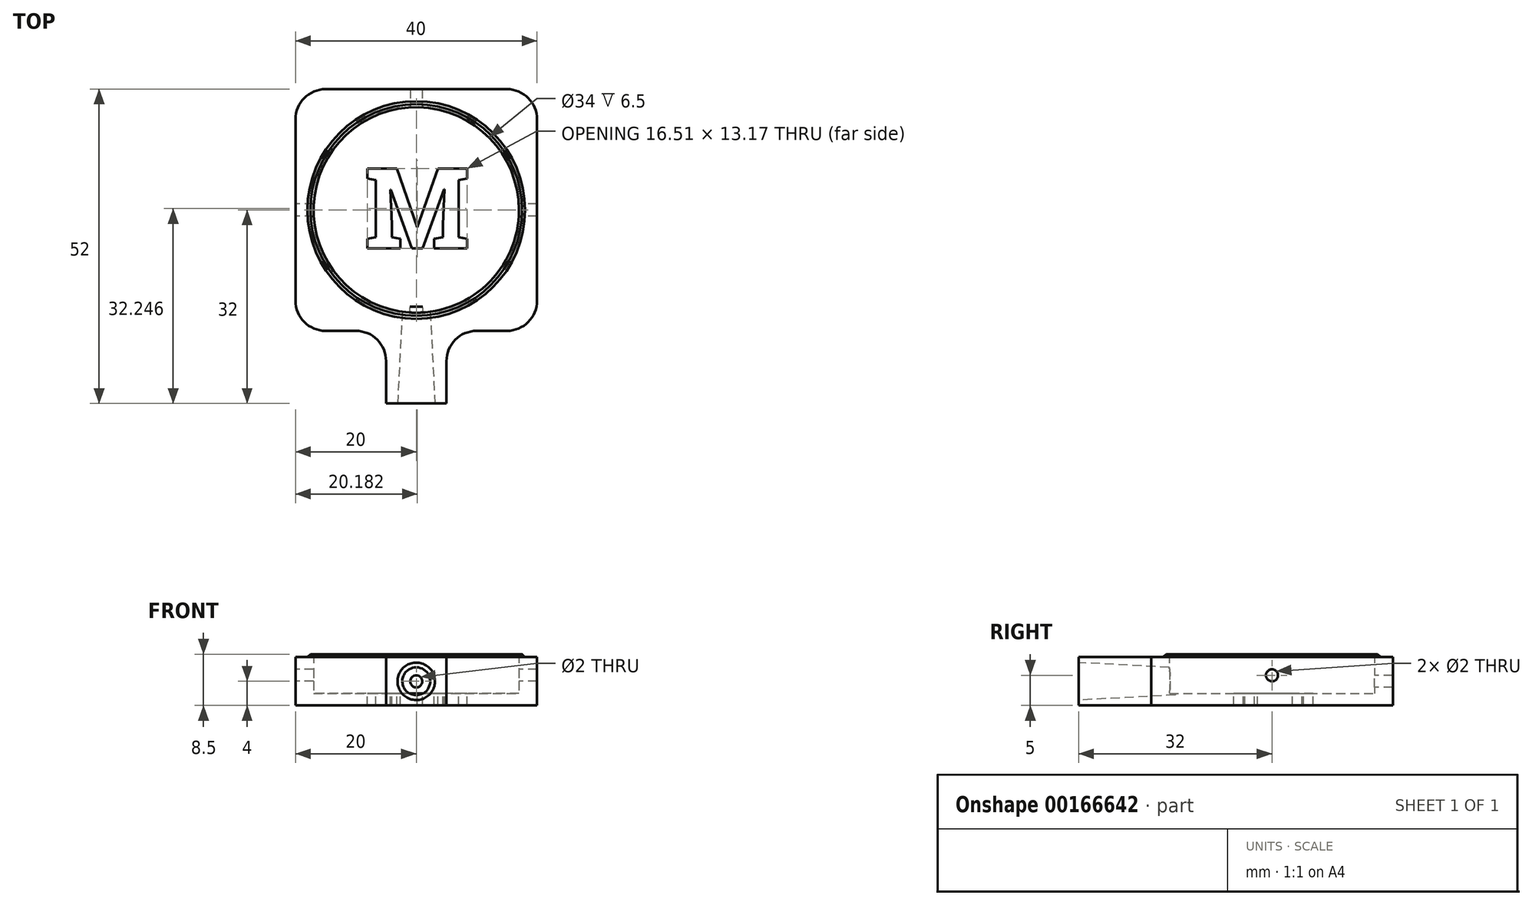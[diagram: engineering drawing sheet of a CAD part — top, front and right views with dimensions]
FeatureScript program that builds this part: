
annotation { "Feature Type Name" : "Feature", "Feature Type Description" : "" }
export const myFeature = defineFeature(function(context is Context, id is Id, definition is map)
    precondition{}
    {
        {
            var Q0;
            Q0=qCreatedBy(makeId("Top.planeOp"),FACE);
            var sketch = newSketch(context, id + "F0", { "sketchPlane" : qUnion([Q0])});
            skLineSegment(sketch, "E0.bottom", {"start": v(-15, 20) * mm, "end": v(15, 20) * mm});
            skLineSegment(sketch, "E0.top", {"start": v(-15, -20) * mm, "end": v(-10, -20) * mm});
            skLineSegment(sketch, "E0.left", {"start": v(-20, 15) * mm, "end": v(-20, -15) * mm});
            skLineSegment(sketch, "E0.right", {"start": v(20, 15) * mm, "end": v(20, -15) * mm});
            skPoint(sketch, "E1.visualSharp", {"position": v(-20, 20) * mm});
            skArc(sketch, "E1.filletArc", {"start": v(-15, 20) * mm, "mid": v(-18.54, 18.54) * mm, "end": v(-20, 15) * mm});
            skPoint(sketch, "E2.visualSharp", {"position": v(20, 20) * mm});
            skArc(sketch, "E2.filletArc", {"start": v(20, 15) * mm, "mid": v(18.54, 18.54) * mm, "end": v(15, 20) * mm});
            skPoint(sketch, "E3.visualSharp", {"position": v(20, -20) * mm});
            skArc(sketch, "E3.filletArc", {"start": v(15, -20) * mm, "mid": v(18.54, -18.54) * mm, "end": v(20, -15) * mm});
            skPoint(sketch, "E4.visualSharp", {"position": v(-20, -20) * mm});
            skArc(sketch, "E4.filletArc", {"start": v(-20, -15) * mm, "mid": v(-18.54, -18.54) * mm, "end": v(-15, -20) * mm});
            skText(sketch, "E5", { "text": "M", "fontName": "RobotoSlab-Bold.ttf"});
            skCircle(sketch, "E6", {"center": v(0, 0) * mm, "radius": 17 * mm});
            skLineSegment(sketch, "E7.bottom", {"start": v(-5, -20) * mm, "end": v(5, -20) * mm});
            skLineSegment(sketch, "E7.top", {"start": v(-5, -32) * mm, "end": v(5, -32) * mm});
            skLineSegment(sketch, "E7.left", {"start": v(-5, -25) * mm, "end": v(-5, -32) * mm});
            skLineSegment(sketch, "E7.right", {"start": v(5, -25) * mm, "end": v(5, -32) * mm});
            skArc(sketch, "E8.filletArc", {"start": v(-5, -25) * mm, "mid": v(-6.46, -21.46) * mm, "end": v(-10, -20) * mm});
            skLineSegment(sketch, "E9", {"start": v(10, -20) * mm, "end": v(15, -20) * mm});
            skPoint(sketch, "E10.visualSharp", {"position": v(5, -20) * mm});
            skArc(sketch, "E10.filletArc", {"start": v(10, -20) * mm, "mid": v(6.46, -21.46) * mm, "end": v(5, -25) * mm});
            skCircle(sketch, "E11", {"center": v(0, 0) * mm, "radius": 18 * mm});
            const initialGuessF0  = {"E5": [-0.00858, -0.00634, 1, 0, 0.01334]};
            skSetInitialGuess(sketch, initialGuessF0);
            skSolve(sketch);
        }
        {
            var Q0;
            Q0=makeQuery(id+"F0.imprint","IMPRINT",FACE,{"disambiguationData":[TD([[makeQuery(id+"F0.imprint","IMPRINT",EDGE,{"derivedFrom":sQuery(id+"F0.wireOp",EDGE,"E0.bottom")}),-1.0]])]});
            var Q1;
            Q1=makeQuery(id+"F0.imprint","IMPRINT",FACE,{"disambiguationData":[TD([[makeQuery(id+"F0.imprint","IMPRINT",EDGE,{"derivedFrom":sQuery(id+"F0.wireOp",EDGE,"E5.sketch_text.stroke-0")}),1.0]])]});
            var Q2;
            Q2=makeQuery(id+"F0.imprint","IMPRINT",FACE,{"disambiguationData":[TD([[makeQuery(id+"F0.imprint","IMPRINT",EDGE,{"derivedFrom":sQuery(id+"F0.wireOp",EDGE,"E5.sketch_text.stroke-0")}),-1.0]])]});
            var Q3;
            Q3=makeQuery(id+"F0.imprint","IMPRINT",FACE,{"disambiguationData":[TD([[makeQuery(id+"F0.imprint","IMPRINT",EDGE,{"derivedFrom":sQuery(id+"F0.wireOp",EDGE,"E6")}),-1.0]])]});
            extrude(context, id + "F1", {"entities" : qUnion([Q0, Q1, Q2, Q3]), "oppositeDirection" : true, "depth" : 2 * mm});
        }
        {
            var Q0;
            Q0=makeQuery(id+"F0.imprint","IMPRINT",FACE,{"disambiguationData":[TD([[makeQuery(id+"F0.imprint","IMPRINT",EDGE,{"derivedFrom":sQuery(id+"F0.wireOp",EDGE,"E0.bottom")}),-1.0]])]});
            extrude(context, id + "F2", {"entities" : qUnion([Q0]), "operationType" : NewBodyOperationType.ADD, "depth" : 6 * mm});
        }
        {
            var Q0;
            Q0=makeQuery(id+"F0.imprint","IMPRINT",FACE,{"disambiguationData":[TD([[makeQuery(id+"F0.imprint","IMPRINT",EDGE,{"derivedFrom":sQuery(id+"F0.wireOp",EDGE,"E5.sketch_text.stroke-0")}),-1.0]])]});
            extrude(context, id + "F3", {"entities" : qUnion([Q0]), "operationType" : NewBodyOperationType.REMOVE, "oppositeDirection" : true, "depth" : 2 * mm});
        }
        {
            var Q0;
            Q0=makeQuery(id+"F0.imprint","IMPRINT",FACE,{"disambiguationData":[TD([[makeQuery(id+"F0.imprint","IMPRINT",EDGE,{"derivedFrom":sQuery(id+"F0.wireOp",EDGE,"E6")}),-1.0]])]});
            extrude(context, id + "F4", {"entities" : qUnion([Q0]), "operationType" : NewBodyOperationType.ADD, "depth" : 6.5 * mm});
        }
        {
            var Q0;
            {var subQ0=sQuery(id+"F0.wireOp",EDGE,"E7.top");Q0=makeQuery(id+"F2.boolean.opBoolean","MERGE",FACE,{"derivedFrom":[makeQuery(id+"F1.opExtrude","SWEPT_FACE",FACE,{"disambiguationData":[OSD([subQ0])]}),makeQuery(id+"F2.opExtrude","SWEPT_FACE",FACE,{"disambiguationData":[OSD([subQ0])]})]});}
            var sketch = newSketch(context, id + "F5", { "sketchPlane" : qUnion([Q0])});
            skCircle(sketch, "E12", {"center": v(0, 2) * mm, "radius": 3.1 * mm});
            skPoint(sketch, "E12.centerSnap0", {"position": v(-5, 2) * mm});
            skPoint(sketch, "E12.centerSnap1", {"position": v(0, 6) * mm});
            skCircle(sketch, "E13", {"center": v(0, 2) * mm, "radius": 1 * mm});
            skSolve(sketch);
        }
        {
            var Q0;
            Q0=makeQuery(id+"F5.imprint","IMPRINT",FACE,{"disambiguationData":[TD([[makeQuery(id+"F5.imprint","IMPRINT",EDGE,{"derivedFrom":sQuery(id+"F5.wireOp",EDGE,"E12")}),1.0]])]});
            var Q1;
            Q1=makeQuery(id+"F5.imprint","IMPRINT",FACE,{"disambiguationData":[TD([[makeQuery(id+"F5.imprint","IMPRINT",EDGE,{"derivedFrom":sQuery(id+"F5.wireOp",EDGE,"E13")}),1.0]])]});
            extrude(context, id + "F6", {"entities" : qUnion([Q0, Q1]), "operationType" : NewBodyOperationType.REMOVE, "oppositeDirection" : true, "depth" : 16 * mm, "hasDraft" : true, "draftAngle" : 3 * degree, "draftPullDirection" : true});
        }
        {
            var Q0;
            {var subQ0=sQuery(id+"F0.wireOp",EDGE,"E0.left");Q0=makeQuery(id+"F2.boolean.opBoolean","MERGE",FACE,{"derivedFrom":[makeQuery(id+"F1.opExtrude","SWEPT_FACE",FACE,{"disambiguationData":[OSD([subQ0])]}),makeQuery(id+"F2.opExtrude","SWEPT_FACE",FACE,{"disambiguationData":[OSD([subQ0])]})]});}
            var sketch = newSketch(context, id + "F7", { "sketchPlane" : qUnion([Q0])});
            skCircle(sketch, "E14", {"center": v(0, 3) * mm, "radius": 1 * mm});
            skPoint(sketch, "E14.centerSnap0", {"position": v(0, -2) * mm});
            skSolve(sketch);
        }
        {
            var Q0;
            Q0 = qSketchRegion(id + "F7", true);
            var Q1;
            {var subQ0=sQuery(id+"F0.wireOp",EDGE,"E0.right");Q1=makeQuery(id+"F2.boolean.opBoolean","MERGE",FACE,{"derivedFrom":[makeQuery(id+"F1.opExtrude","SWEPT_FACE",FACE,{"disambiguationData":[OSD([subQ0])]}),makeQuery(id+"F2.opExtrude","SWEPT_FACE",FACE,{"disambiguationData":[OSD([subQ0])]})]});}
            extrude(context, id + "F8", {"entities" : qUnion([Q0]), "operationType" : NewBodyOperationType.REMOVE, "endBound" : BoundingType.UP_TO_SURFACE, "oppositeDirection" : true, "endBoundEntityFace" : qUnion([Q1]), "depth" : 25 * mm});
        }
        {
            var Q0;
            Q0=makeQuery(id+"F5.imprint","IMPRINT",FACE,{"disambiguationData":[TD([[makeQuery(id+"F5.imprint","IMPRINT",EDGE,{"derivedFrom":sQuery(id+"F5.wireOp",EDGE,"E13")}),1.0]])]});
            var Q1;
            {var subQ0=sQuery(id+"F0.wireOp",EDGE,"E0.bottom");Q1=makeQuery(id+"F2.boolean.opBoolean","MERGE",FACE,{"derivedFrom":[makeQuery(id+"F1.opExtrude","SWEPT_FACE",FACE,{"disambiguationData":[OSD([subQ0])]}),makeQuery(id+"F2.opExtrude","SWEPT_FACE",FACE,{"disambiguationData":[OSD([subQ0])]})]});}
            extrude(context, id + "F9", {"entities" : qUnion([Q0]), "operationType" : NewBodyOperationType.REMOVE, "endBound" : BoundingType.UP_TO_SURFACE, "oppositeDirection" : true, "endBoundEntityFace" : qUnion([Q1]), "depth" : 25 * mm});
        }
        {
            var Q0;
            Q0=makeQuery(id+"F4.opExtrude","CAP_EDGE",EDGE,{"disambiguationData":[OSD([sQuery(id+"F0.wireOp",EDGE,"E11")])],"isStart":false});
            chamfer(context, id + "F10", {"entities" : qUnion([Q0]), "width" : 0.5 * mm, "tangentPropagation" : true});
        }
    });
